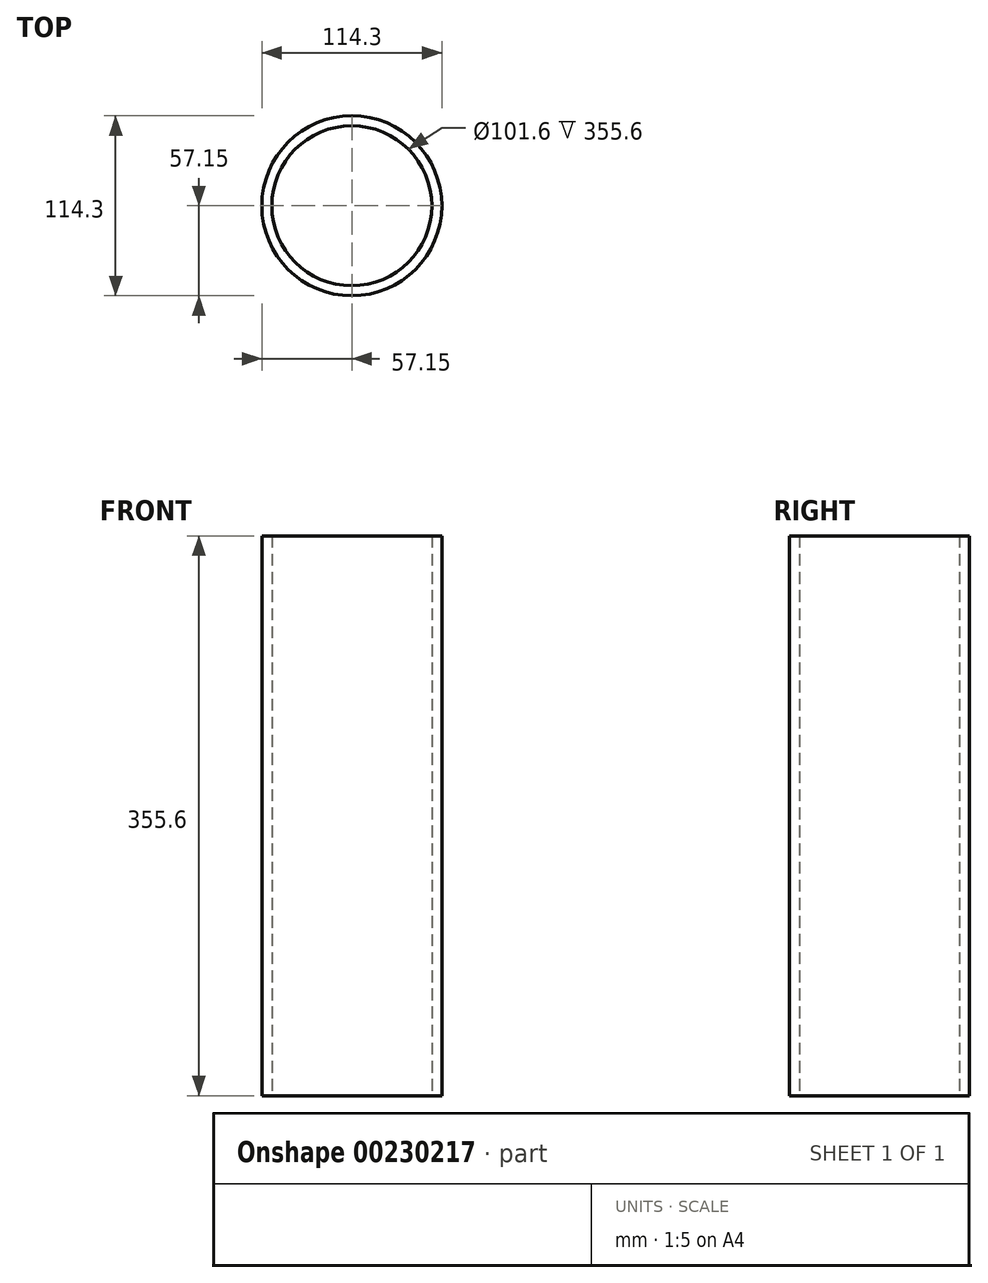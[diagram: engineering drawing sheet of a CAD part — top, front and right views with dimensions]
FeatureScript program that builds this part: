
annotation { "Feature Type Name" : "Feature", "Feature Type Description" : "" }
export const myFeature = defineFeature(function(context is Context, id is Id, definition is map)
    precondition{}
    {
        {
            var Q0;
            Q0=qCreatedBy(makeId("Top.planeOp"),FACE);
            var sketch = newSketch(context, id + "F0", { "sketchPlane" : qUnion([Q0])});
            skCircle(sketch, "E0", {"center": v(0, 0) * mm, "radius": 57.15 * mm});
            skCircle(sketch, "E1", {"center": v(0, 0) * mm, "radius": 50.8 * mm});
            skSolve(sketch);
        }
        {
            var Q0;
            Q0 = qSketchRegion(id + "F0", true);
            extrude(context, id + "F1", {"entities" : qUnion([Q0]), "depth" : 355.6 * mm});
        }
    });
